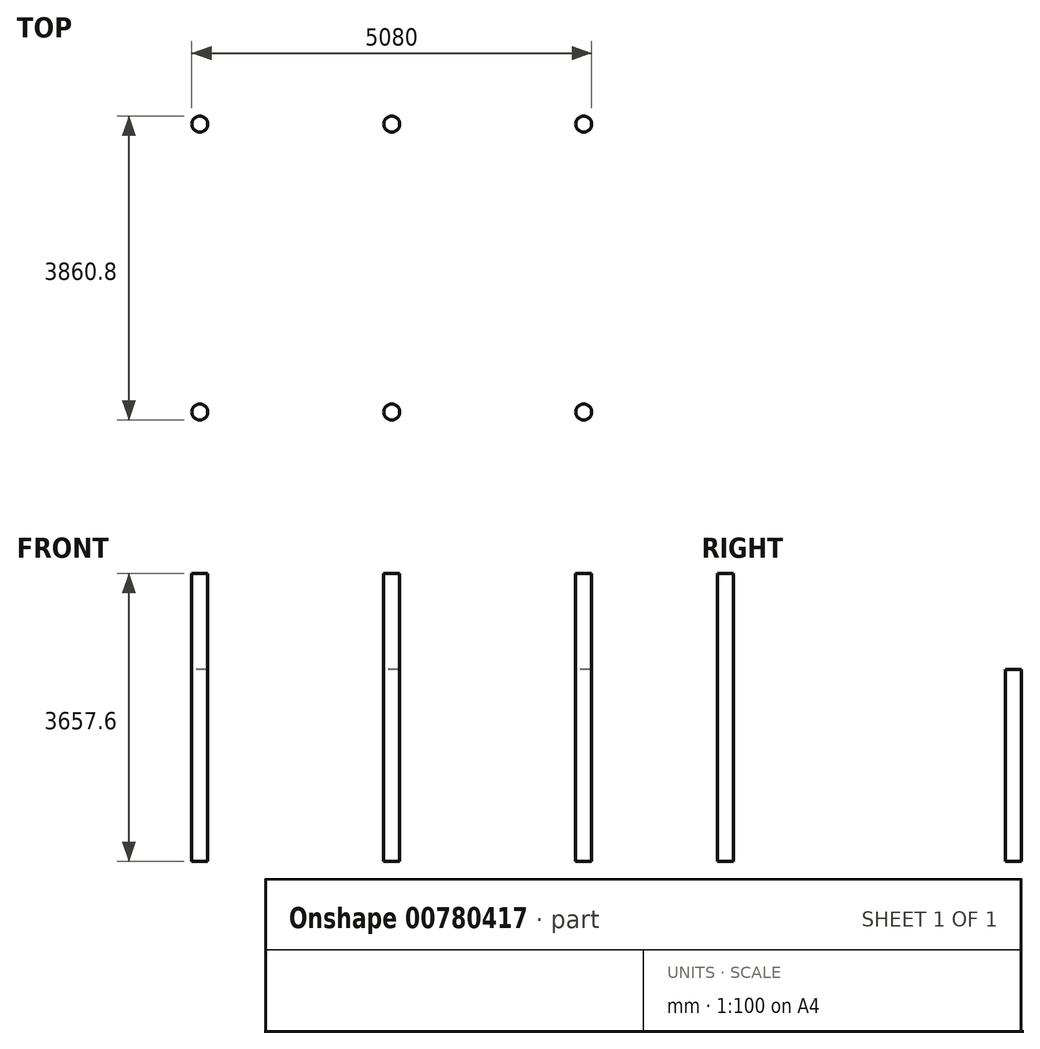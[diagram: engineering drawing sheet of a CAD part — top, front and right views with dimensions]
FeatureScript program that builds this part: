
annotation { "Feature Type Name" : "Feature", "Feature Type Description" : "" }
export const myFeature = defineFeature(function(context is Context, id is Id, definition is map)
    precondition{}
    {
        {
            var Q0;
            Q0=qCreatedBy(makeId("Top.planeOp"),FACE);
            var sketch = newSketch(context, id + "F0", { "sketchPlane" : qUnion([Q0])});
            skCircle(sketch, "E0", {"center": v(-105.74, -40.36) * mm, "radius": 101.6 * mm});
            skSolve(sketch);
        }
        {
            var Q0;
            Q0=makeQuery(id+"F0.imprint","IMPRINT",FACE,{"disambiguationData":[TD([[makeQuery(id+"F0.imprint","IMPRINT",EDGE,{"derivedFrom":sQuery(id+"F0.wireOp",EDGE,"E0")}),1.0]])]});
            var Q1;
            Q1=sQuery(id+"F0.wireOp",EDGE,"E0");
            extrude(context, id + "F1", {"entities" : qUnion([Q0]), "surfaceEntities" : qUnion([Q1]), "depth" : 3657.6 * mm, "offsetDistance" : 25.4 * mm});
        }
        {
            var Q0;
            Q0=makeQuery(id+"F1.opExtrude","SWEPT_BODY",BODY,{"disambiguationData":[OSD([sQuery(id+"F0.wireOp",EDGE,"E0")])]});
            transform(context, id + "F2", {"entities" : qUnion([Q0]), "transformType" : TransformType.TRANSLATION_3D, "dx" : 2438.4 * mm, "dy" : 0 * mm, "dz" : 0 * mm, "makeCopy" : true});
        }
        {
            var Q0;
            Q0=makeQuery(id+"F2.opPattern","COPY",BODY,{"derivedFrom":makeQuery(id+"F1.opExtrude","SWEPT_BODY",BODY,{"disambiguationData":[OSD([sQuery(id+"F0.wireOp",EDGE,"E0")])]}),"instanceName":"1"});
            transform(context, id + "F3", {"entities" : qUnion([Q0]), "transformType" : TransformType.TRANSLATION_3D, "dx" : 2438.4 * mm, "dy" : 0 * mm, "dz" : 0 * mm, "makeCopy" : true});
        }
        {
            var Q0;
            Q0=makeQuery(id+"F1.opExtrude","SWEPT_BODY",BODY,{"disambiguationData":[OSD([sQuery(id+"F0.wireOp",EDGE,"E0")])]});
            transform(context, id + "F4", {"entities" : qUnion([Q0]), "transformType" : TransformType.TRANSLATION_3D, "dx" : 0 * mm, "dy" : 3657.6 * mm, "dz" : 0 * mm, "makeCopy" : true});
        }
        {
            var Q0;
            Q0 = qSketchRegion(id + "F0", true);
            extrude(context, id + "F5", {"entities" : qUnion([Q0]), "depth" : 2438.4 * mm, "offsetDistance" : 25.4 * mm});
        }
        {
            var Q0;
            Q0=makeQuery(id+"F4.opPattern","COPY",BODY,{"derivedFrom":makeQuery(id+"F1.opExtrude","SWEPT_BODY",BODY,{"disambiguationData":[OSD([sQuery(id+"F0.wireOp",EDGE,"E0")])]}),"instanceName":"1"});
            deleteBodies(context, id + "F6", {"entities" : qUnion([Q0])});
        }
        {
            var Q0;
            Q0=makeQuery(id+"F5.opExtrude","SWEPT_BODY",BODY,{"disambiguationData":[OSD([sQuery(id+"F0.wireOp",EDGE,"E0")])]});
            transform(context, id + "F7", {"entities" : qUnion([Q0]), "transformType" : TransformType.TRANSLATION_3D, "dx" : 0 * mm, "dy" : 3657.6 * mm, "dz" : 0 * mm, "makeCopy" : false});
        }
        {
            var Q0;
            Q0=makeQuery(id+"F5.opExtrude","SWEPT_BODY",BODY,{"disambiguationData":[OSD([sQuery(id+"F0.wireOp",EDGE,"E0")])]});
            transform(context, id + "F8", {"entities" : qUnion([Q0]), "transformType" : TransformType.TRANSLATION_3D, "dx" : 2438.4 * mm, "dy" : 0 * mm, "dz" : 0 * mm, "makeCopy" : true});
        }
        {
            var Q0;
            Q0=makeQuery(id+"F8.opPattern","COPY",BODY,{"derivedFrom":makeQuery(id+"F5.opExtrude","SWEPT_BODY",BODY,{"disambiguationData":[OSD([sQuery(id+"F0.wireOp",EDGE,"E0")])]}),"instanceName":"1"});
            transform(context, id + "F9", {"entities" : qUnion([Q0]), "transformType" : TransformType.TRANSLATION_3D, "dx" : 2438.4 * mm, "dy" : 0 * mm, "dz" : 0 * mm, "makeCopy" : true});
        }
    });
